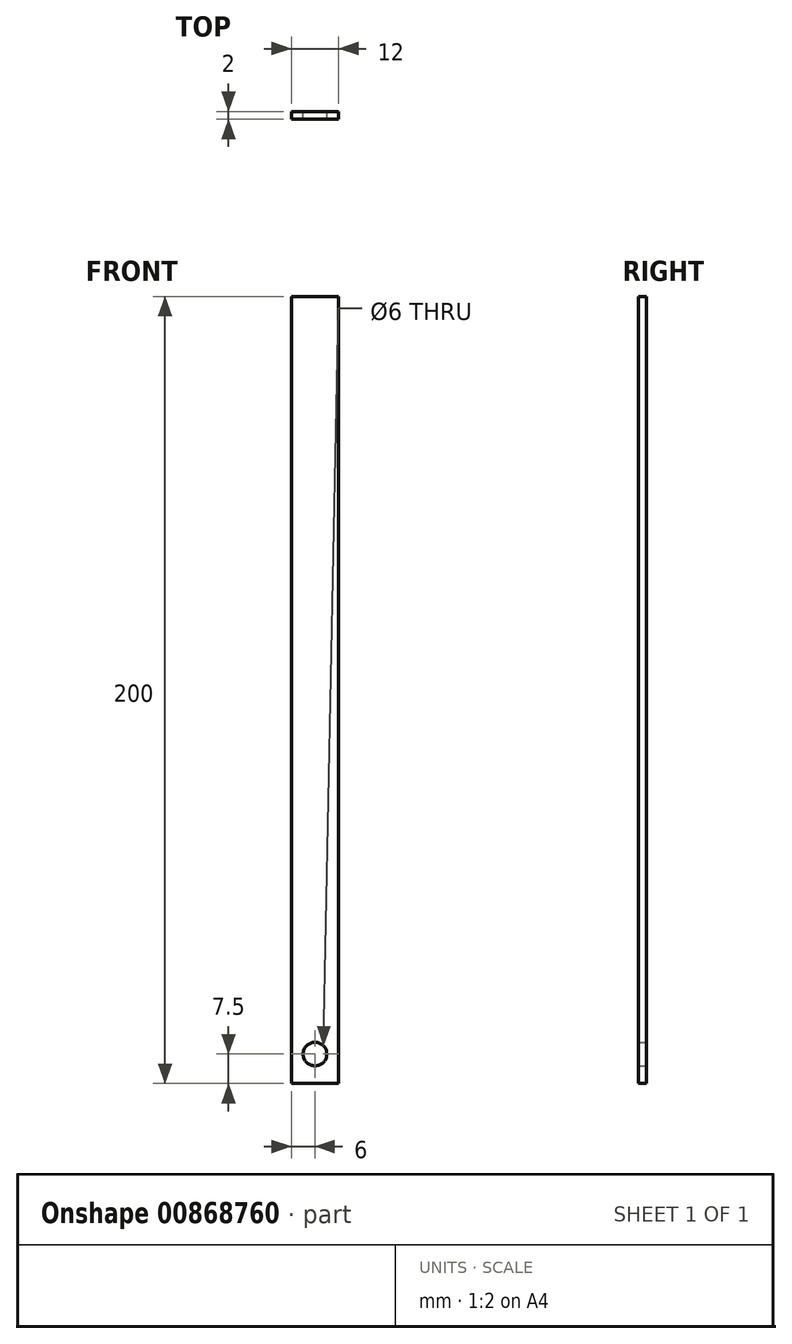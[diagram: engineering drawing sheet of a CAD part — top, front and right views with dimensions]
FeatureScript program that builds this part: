
annotation { "Feature Type Name" : "Feature", "Feature Type Description" : "" }
export const myFeature = defineFeature(function(context is Context, id is Id, definition is map)
    precondition{}
    {
        {
            var Q0;
            Q0=qCreatedBy(makeId("Front.planeOp"),FACE);
            var sketch = newSketch(context, id + "F0", { "sketchPlane" : qUnion([Q0])});
            skLineSegment(sketch, "E0.bottom", {"start": v(-6, 0) * mm, "end": v(6, 0) * mm});
            skLineSegment(sketch, "E0.top", {"start": v(-6, 200) * mm, "end": v(6, 200) * mm});
            skLineSegment(sketch, "E0.left", {"start": v(-6, 0) * mm, "end": v(-6, 200) * mm});
            skLineSegment(sketch, "E0.right", {"start": v(6, 0) * mm, "end": v(6, 200) * mm});
            skCircle(sketch, "E1", {"center": v(0, 7.5) * mm, "radius": 3 * mm});
            skSolve(sketch);
        }
        {
            var Q0;
            Q0=makeQuery(id+"F0.imprint","IMPRINT",FACE,{"disambiguationData":[TD([[makeQuery(id+"F0.imprint","IMPRINT",EDGE,{"derivedFrom":sQuery(id+"F0.wireOp",EDGE,"E0.bottom")}),1.0]])]});
            extrude(context, id + "F1", {"entities" : qUnion([Q0]), "depth" : 2 * mm, "offsetDistance" : 25 * mm});
        }
    });
